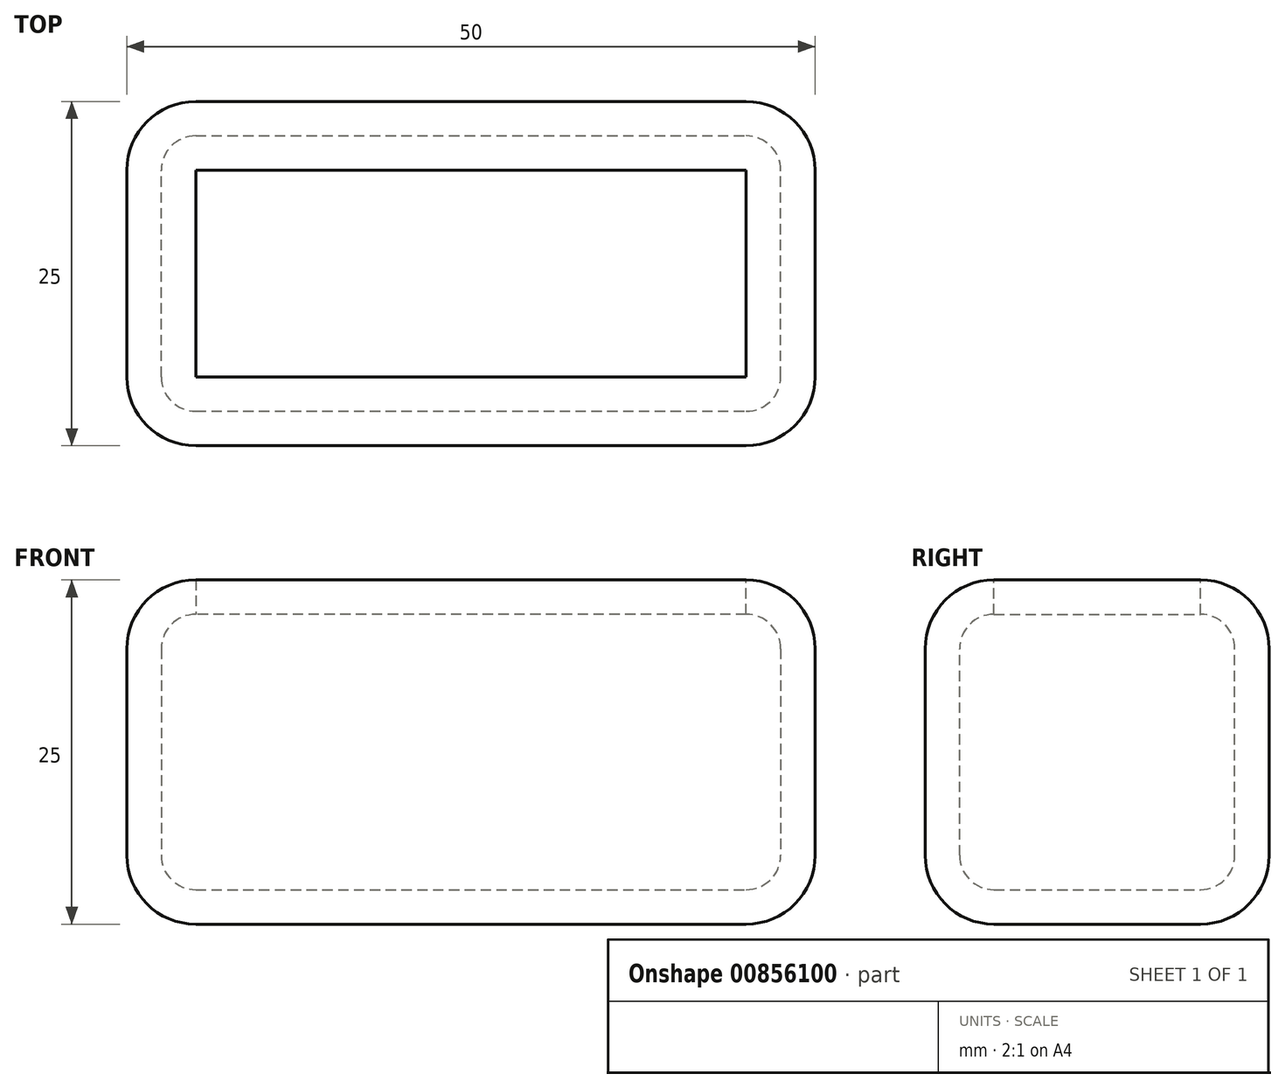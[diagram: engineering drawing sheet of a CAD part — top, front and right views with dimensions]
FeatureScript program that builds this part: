
annotation { "Feature Type Name" : "Feature", "Feature Type Description" : "" }
export const myFeature = defineFeature(function(context is Context, id is Id, definition is map)
    precondition{}
    {
        {
            var Q0;
            Q0=qCreatedBy(makeId("Top.planeOp"),FACE);
            var sketch = newSketch(context, id + "F0", { "sketchPlane" : qUnion([Q0])});
            skLineSegment(sketch, "E0.bottom", {"start": v(-50, 25) * mm, "end": v(0, 25) * mm});
            skLineSegment(sketch, "E0.top", {"start": v(-50, 0) * mm, "end": v(0, 0) * mm});
            skLineSegment(sketch, "E0.left", {"start": v(-50, 25) * mm, "end": v(-50, 0) * mm});
            skLineSegment(sketch, "E0.right", {"start": v(0, 25) * mm, "end": v(0, 0) * mm});
            skSolve(sketch);
        }
        {
            var Q0;
            Q0 = qSketchRegion(id + "F0", true);
            extrude(context, id + "F1", {"entities" : qUnion([Q0]), "depth" : 25 * mm, "offsetDistance" : 25 * mm});
        }
        {
            var Q0;
            Q0=makeQuery(id+"F1.opExtrude","CAP_EDGE",EDGE,{"disambiguationData":[OSD([sQuery(id+"F0.wireOp",EDGE,"E0.right")])],"isStart":false});
            var Q1;
            Q1=makeQuery(id+"F1.opExtrude","CAP_EDGE",EDGE,{"disambiguationData":[OSD([sQuery(id+"F0.wireOp",EDGE,"E0.top")])],"isStart":false});
            var Q2;
            Q2=makeQuery(id+"F1.opExtrude","CAP_EDGE",EDGE,{"disambiguationData":[OSD([sQuery(id+"F0.wireOp",EDGE,"E0.left")])],"isStart":false});
            var Q3;
            Q3=makeQuery(id+"F1.opExtrude","CAP_EDGE",EDGE,{"disambiguationData":[OSD([sQuery(id+"F0.wireOp",EDGE,"E0.bottom")])],"isStart":false});
            var Q4;
            Q4=makeQuery(id+"F1.opExtrude","SWEPT_EDGE",EDGE,{"disambiguationData":[OSD([sQuery(id+"F0.wireOp",EDGE,"E0.bottom"),sQuery(id+"F0.wireOp",EDGE,"E0.left")])]});
            var Q5;
            Q5=makeQuery(id+"F1.opExtrude","CAP_EDGE",EDGE,{"disambiguationData":[OSD([sQuery(id+"F0.wireOp",EDGE,"E0.left")])],"isStart":true});
            var Q6;
            Q6=makeQuery(id+"F1.opExtrude","SWEPT_EDGE",EDGE,{"disambiguationData":[OSD([sQuery(id+"F0.wireOp",EDGE,"E0.top"),sQuery(id+"F0.wireOp",EDGE,"E0.left")])]});
            var Q7;
            Q7=makeQuery(id+"F1.opExtrude","CAP_EDGE",EDGE,{"disambiguationData":[OSD([sQuery(id+"F0.wireOp",EDGE,"E0.top")])],"isStart":true});
            var Q8;
            Q8=makeQuery(id+"F1.opExtrude","CAP_EDGE",EDGE,{"disambiguationData":[OSD([sQuery(id+"F0.wireOp",EDGE,"E0.right")])],"isStart":true});
            var Q9;
            Q9=makeQuery(id+"F1.opExtrude","CAP_EDGE",EDGE,{"disambiguationData":[OSD([sQuery(id+"F0.wireOp",EDGE,"E0.bottom")])],"isStart":true});
            var Q10;
            Q10=makeQuery(id+"F1.opExtrude","SWEPT_EDGE",EDGE,{"disambiguationData":[OSD([sQuery(id+"F0.wireOp",EDGE,"E0.bottom"),sQuery(id+"F0.wireOp",EDGE,"E0.right")])]});
            var Q11;
            Q11=makeQuery(id+"F1.opExtrude","SWEPT_EDGE",EDGE,{"disambiguationData":[OSD([sQuery(id+"F0.wireOp",EDGE,"E0.top"),sQuery(id+"F0.wireOp",EDGE,"E0.right")])]});
            fillet(context, id + "F2", {"entities" : qUnion([Q0, Q1, Q2, Q3, Q4, Q5, Q6, Q7, Q8, Q9, Q10, Q11]), "radius" : 5 * mm, "tangentPropagation" : true, "allowEdgeOverflow" : false});
        }
        {
            var Q0;
            Q0=makeQuery(id+"F1.opExtrude","CAP_FACE",FACE,{"disambiguationData":[OSD([sQuery(id+"F0.wireOp",EDGE,"E0.bottom"),sQuery(id+"F0.wireOp",EDGE,"E0.top"),sQuery(id+"F0.wireOp",EDGE,"E0.left"),sQuery(id+"F0.wireOp",EDGE,"E0.right")])],"isStart":false});
            shell(context, id + "F3", {"entities" : qUnion([Q0]), "thickness" : 2.5 * mm});
        }
    });
